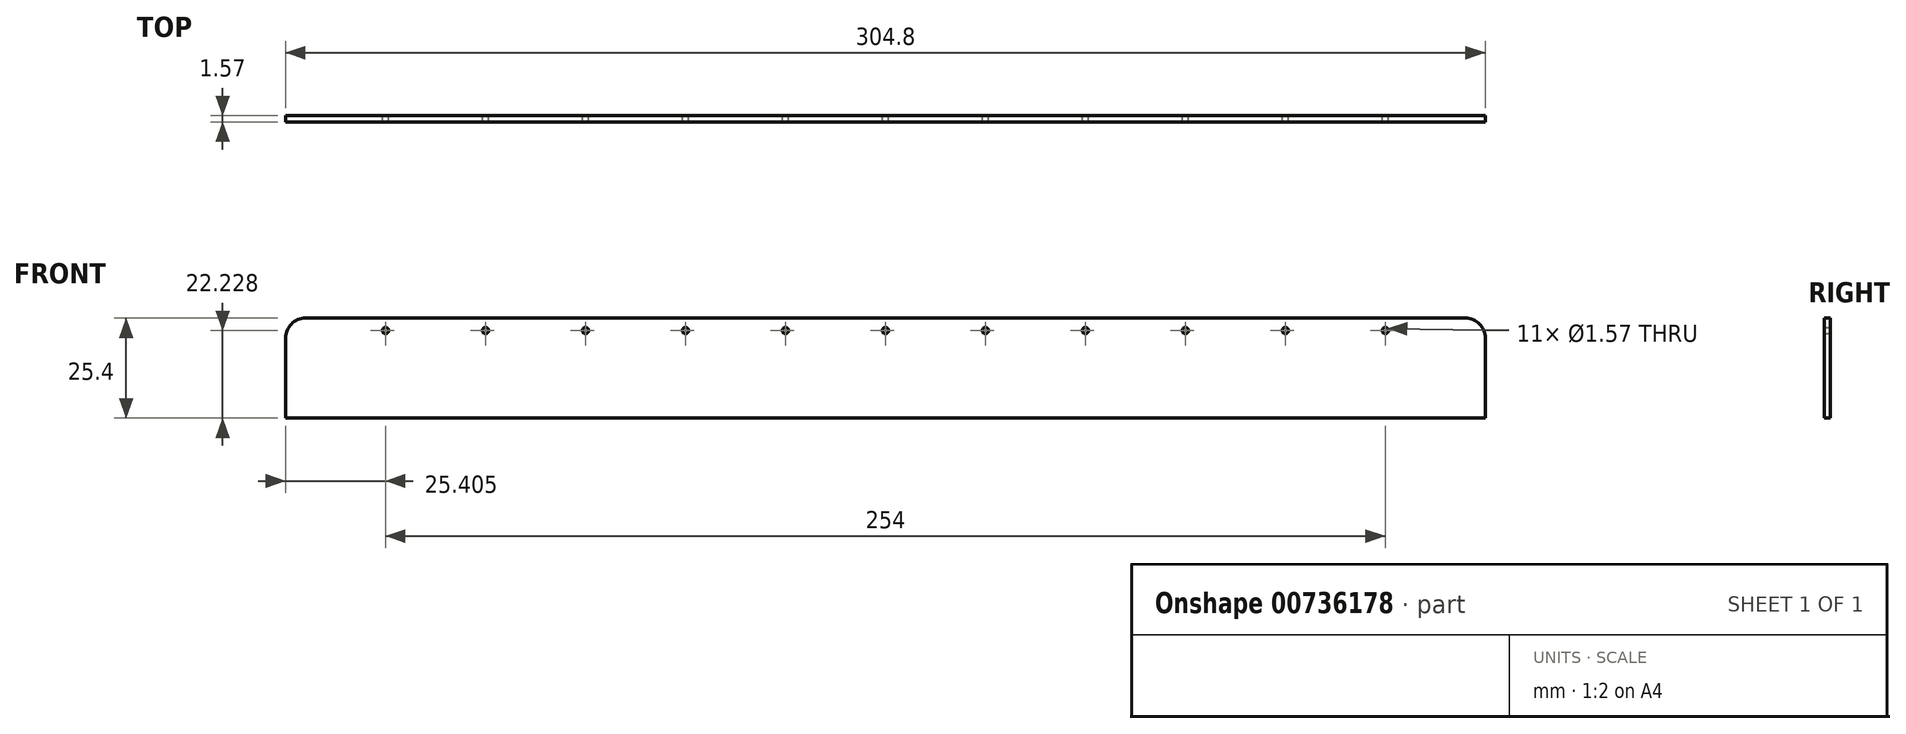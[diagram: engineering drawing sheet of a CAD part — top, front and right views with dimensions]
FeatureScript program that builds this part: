
annotation { "Feature Type Name" : "Feature", "Feature Type Description" : "" }
export const myFeature = defineFeature(function(context is Context, id is Id, definition is map)
    precondition{}
    {
        {
            var Q0;
            Q0=qCreatedBy(makeId("Front.planeOp"),FACE);
            var sketch = newSketch(context, id + "F0", { "sketchPlane" : qUnion([Q0])});
            skLineSegment(sketch, "E0.bottom", {"start": v(-56.76, 21.74) * mm, "end": v(248.04, 21.74) * mm});
            skLineSegment(sketch, "E0.top", {"start": v(-56.76, -3.66) * mm, "end": v(248.04, -3.66) * mm});
            skLineSegment(sketch, "E0.left", {"start": v(-56.76, 21.74) * mm, "end": v(-56.76, -3.66) * mm});
            skLineSegment(sketch, "E0.right", {"start": v(248.04, 21.74) * mm, "end": v(248.04, -3.66) * mm});
            skCircle(sketch, "E1", {"center": v(-31.36, 18.57) * mm, "radius": 0.79 * mm});
            skCircle(sketch, "E2", {"center": v(-5.96, 18.57) * mm, "radius": 0.79 * mm});
            skCircle(sketch, "E3", {"center": v(19.44, 18.57) * mm, "radius": 0.79 * mm});
            skCircle(sketch, "E4", {"center": v(44.84, 18.57) * mm, "radius": 0.79 * mm});
            skCircle(sketch, "E5", {"center": v(70.24, 18.57) * mm, "radius": 0.79 * mm});
            skCircle(sketch, "E6", {"center": v(95.64, 18.57) * mm, "radius": 0.79 * mm});
            skCircle(sketch, "E7", {"center": v(121.04, 18.57) * mm, "radius": 0.79 * mm});
            skCircle(sketch, "E8", {"center": v(146.44, 18.57) * mm, "radius": 0.79 * mm});
            skCircle(sketch, "E9", {"center": v(171.84, 18.57) * mm, "radius": 0.79 * mm});
            skCircle(sketch, "E10", {"center": v(197.24, 18.57) * mm, "radius": 0.79 * mm});
            skCircle(sketch, "E11", {"center": v(222.64, 18.57) * mm, "radius": 0.79 * mm});
            skSolve(sketch);
        }
        {
            var Q0;
            Q0=makeQuery(id+"F0.imprint","IMPRINT",FACE,{"disambiguationData":[TD([[makeQuery(id+"F0.imprint","IMPRINT",EDGE,{"derivedFrom":sQuery(id+"F0.wireOp",EDGE,"E0.bottom")}),-1.0]])]});
            extrude(context, id + "F1", {"entities" : qUnion([Q0]), "depth" : 1.57 * mm, "offsetDistance" : 25.4 * mm});
        }
        {
            var Q0;
            Q0=makeQuery(id+"F1.opExtrude","SWEPT_EDGE",EDGE,{"disambiguationData":[OSD([sQuery(id+"F0.wireOp",EDGE,"E0.bottom"),sQuery(id+"F0.wireOp",EDGE,"E0.right")])]});
            var Q1;
            Q1=makeQuery(id+"F1.opExtrude","SWEPT_EDGE",EDGE,{"disambiguationData":[OSD([sQuery(id+"F0.wireOp",EDGE,"E0.bottom"),sQuery(id+"F0.wireOp",EDGE,"E0.left")])]});
            fillet(context, id + "F2", {"entities" : qUnion([Q0, Q1]), "radius" : 5.08 * mm, "tangentPropagation" : true, "allowEdgeOverflow" : false});
        }
    });
